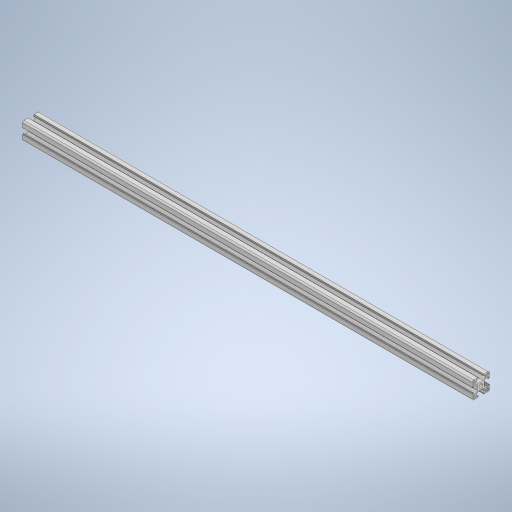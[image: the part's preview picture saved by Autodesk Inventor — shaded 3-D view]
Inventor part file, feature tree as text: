
AUTODESK INVENTOR PART (.ipt)
format: ipt  version: 2023 (Build 270158000, 158)  size: 373,760 bytes
history: native  units: mm
features: extrude x1, mirror x1, pattern_circular x1, sketch x1
ambient origin geometry x8: Origin, YZ Plane, XZ Plane, XY Plane, X Axis, Y Axis, Z Axis, Center Point
bodies: Solid1 (feature_tree)
feature tree (4):
  extrude  "Extrusion1"  TaperAngle=45.0deg  [1 undecoded]
  mirror  "Mirror1"
  pattern_circular  "Circular Pattern1"  Angle=45.0deg  [1 undecoded]
  sketch  "Sketch1"  dims[d0=3.4mm d1=45.0deg d3=45.0deg d4=2.5mm d5=135.0deg d6=1.0mm d7=4.1mm d8=5.2mm d9=8.25mm d10=15.0mm d11=2.2mm d12=5.8mm d13=1.5mm d14=1.5mm d15=1.0mm d16=1.0mm d17=1.0mm d18=780.0mm d19=0.0mm d20=40.0mm d21=360.0deg]
note: 2 required parameter values undecoded (feature->parameter linkage not recoverable at this tier; creation-order binding heuristic only, values carry confidence <= 0.55)
